# Revit family: TV-298
name_source: partatom
category: Aparatos sanitarios
units: mm (PartAtom-declared; Revit-internal decimal feet)

## family parameters
Compartido = No
Corte con vacíos al cargar = No
Cota de conector redondo = Diámetro de uso
Número OmniClass = 23.45.00.00
Punto de cálculo de habitación = No
Se basa en plano de trabajo = No
Siempre vertical = Sí
Tipo de pieza = Normal
Título OmniClass = Sanitary, Laundry, and Cleaning Equipment

## types (1)
- TV-298
    Batteries = DL-223 Duracell Lithium Battery or Panasonic CR-P2
    Certification = http://www.helvex.com.mx
    Chrome = Brass Chrome
    Comentarios de tipo = Electronic Line
    Connection = ½" - 14 NPSM
    Descripción = Omega Electronic Battery Sinlge Faucet For Lavatory
    Detection Range = 1.9" (50 mm) - 8.7" (220 mm)
    Documentation = http://www.helvex.com.mx
    Elevación por defecto = 0"
    Fabricante = HELVEX
    Features = Swivel Outlet, Infrared Sensor, Filter With Check Valve For Maintenance
    Feeding Voltage = 6 V
    Instructive = http://www.helvex.com.mx
    Max. Working Pressure = 85.3 psi
    Min. Working Pressure = 5.7 psi
    Modelo = TV-298
    Total Height = 12"
    Total Length = 6"
    Total Width = 5"
    URL = http://www.helvex.com.mx

## geometry (parser evidence)
native form markers: Sweep x3
no freeform markers — native parametric forms only
